# Revit family: Hand_Shower-GROHE-Tempesta-26047_Series
name_source: partatom
category: Plumbing Fixtures
units: mm (PartAtom-declared; Revit-internal decimal feet)

## family parameters
Always vertical = No
Cut with Voids When Loaded = No
OmniClass Number = 23.45.05.14.17
OmniClass Title = Showers
Part Type = Normal
Room Calculation Point = No
Round Connector Dimension = Use Diameter
Shared = Yes
Work Plane-Based = Yes

## types (2) — shared parameters
Assembly Code = D2010710
CW Connection = No
CWFU = 3
CalGreen Compliant = Yes
Default Elevation = 0"
Description = 110 ROUND HAND SHOWER - 2 SPRAYS, 1.5 GPM
Face Diameter = 4 5/16"
Flow Rate = 1.5gpm (5.7L/min)
HW Connection = No
HWFU = 3
Height = 6 5/16"
Installation Type = Surface Mounted
Manufacturer = Grohe
Tempered Connection Diameter = 1/2"
Tempered Water Connection = Yes
URL = https://www.grohe.us
Vent Connection = No
WFU = 4
Waste Connection = No
Width = 2 15/16"
cUPC Compliant = Yes

## per-type parameters (varying)
| type | Finish | Material |
| 26047002 | Metal-Grohe-002-StarLight Chrome | Metal-Grohe-002-StarLight Chrome |
| 260472432 | Metal-Grohe-2432-Matte Black | Metal-Grohe-2432-Matte Black |

note: column(s) folded — value = type name in every type: Model

## geometry (parser evidence)
native form markers: Sweep x2
no freeform markers — native parametric forms only
